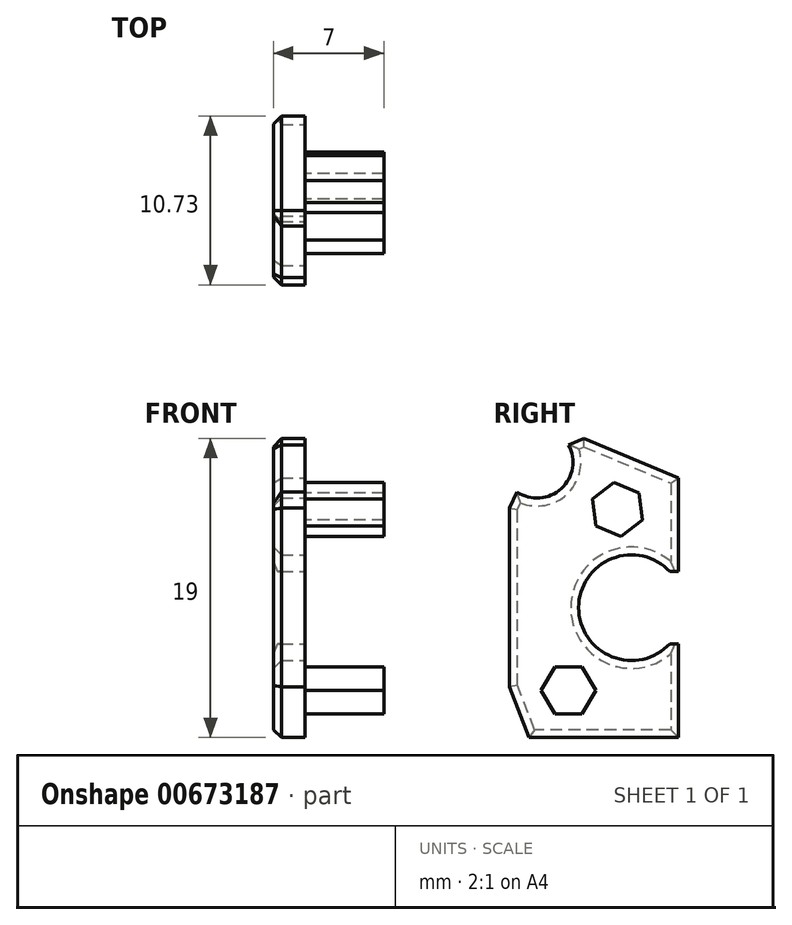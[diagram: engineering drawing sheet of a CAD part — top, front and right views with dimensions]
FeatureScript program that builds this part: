
annotation { "Feature Type Name" : "Feature", "Feature Type Description" : "" }
export const myFeature = defineFeature(function(context is Context, id is Id, definition is map)
    precondition{}
    {
        {
            var Q0;
            Q0=qCreatedBy(makeId("Right.planeOp"),FACE);
            var sketch = newSketch(context, id + "F0", { "sketchPlane" : qUnion([Q0])});
            skCircle(sketch, "E0.cCircle", {"center": v(1.33, 5.27) * mm, "radius": 1.5 * mm, "construction": true});
            skLineSegment(sketch, "E0.0", {"start": v(1.1, 6.99) * mm, "end": v(2.7, 6.32) * mm});
            skLineSegment(sketch, "E0.1", {"start": v(2.7, 6.32) * mm, "end": v(2.92, 4.6) * mm});
            skLineSegment(sketch, "E0.2", {"start": v(2.92, 4.6) * mm, "end": v(1.55, 3.55) * mm});
            skLineSegment(sketch, "E0.3", {"start": v(1.55, 3.55) * mm, "end": v(-0.05, 4.22) * mm});
            skLineSegment(sketch, "E0.4", {"start": v(-0.05, 4.22) * mm, "end": v(-0.27, 5.93) * mm});
            skLineSegment(sketch, "E0.5", {"start": v(-0.27, 5.93) * mm, "end": v(1.1, 6.99) * mm});
            skPoint(sketch, "E0.0.midPoint", {"position": v(1.9, 6.65) * mm});
            skCircle(sketch, "E1.cCircle", {"center": v(-1.8, -6.23) * mm, "radius": 1.5 * mm, "construction": true});
            skLineSegment(sketch, "E1.0", {"start": v(-0.92, -7.73) * mm, "end": v(-2.66, -7.73) * mm});
            skLineSegment(sketch, "E1.1", {"start": v(-2.66, -7.73) * mm, "end": v(-3.52, -6.23) * mm});
            skLineSegment(sketch, "E1.2", {"start": v(-3.52, -6.23) * mm, "end": v(-2.66, -4.73) * mm});
            skLineSegment(sketch, "E1.3", {"start": v(-2.66, -4.73) * mm, "end": v(-0.92, -4.73) * mm});
            skLineSegment(sketch, "E1.4", {"start": v(-0.92, -4.73) * mm, "end": v(-0.06, -6.23) * mm});
            skLineSegment(sketch, "E1.5", {"start": v(-0.06, -6.23) * mm, "end": v(-0.92, -7.73) * mm});
            skPoint(sketch, "E1.0.midPoint", {"position": v(-1.8, -7.73) * mm});
            skLineSegment(sketch, "E2", {"start": v(5.2, 1.3) * mm, "end": v(5.2, 7.27) * mm});
            skLineSegment(sketch, "E3", {"start": v(5.2, 7.27) * mm, "end": v(-0.8, 9.77) * mm});
            skLineSegment(sketch, "E4", {"start": v(-5.52, 5.37) * mm, "end": v(-5.52, -6) * mm});
            skLineSegment(sketch, "E5", {"start": v(-5.52, -6) * mm, "end": v(-4.3, -9.23) * mm});
            skLineSegment(sketch, "E6", {"start": v(-4.3, -9.23) * mm, "end": v(5.2, -9.23) * mm});
            skLineSegment(sketch, "E7", {"start": v(5.2, -9.23) * mm, "end": v(5.2, -3.27) * mm});
            skLineSegment(sketch, "E8", {"start": v(5.2, -3.27) * mm, "end": v(4.66, -3.27) * mm});
            skArc(sketch, "E9", {"start": v(4.66, 1.3) * mm, "mid": v(-1.14, -0.98) * mm, "end": v(4.66, -3.27) * mm});
            skArc(sketch, "E10", {"start": v(-5.05, 6.35) * mm, "mid": v(-2.24, 6.58) * mm, "end": v(-1.77, 9.36) * mm});
            skLineSegment(sketch, "E11", {"start": v(-5.52, 5.37) * mm, "end": v(-5.05, 6.35) * mm});
            skLineSegment(sketch, "E12", {"start": v(-0.8, 9.77) * mm, "end": v(-1.77, 9.36) * mm});
            skLineSegment(sketch, "E13", {"start": v(4.66, 1.3) * mm, "end": v(5.2, 1.3) * mm});
            skSolve(sketch);
        }
        {
            var Q0;
            Q0=qSketchRegion(id+"F0",true);
            var Q1;
            Q1=makeQuery(id+"F0.imprint","IMPRINT",FACE,{"disambiguationData":[TD([[makeQuery(id+"F0.imprint","IMPRINT",EDGE,{"derivedFrom":sQuery(id+"F0.wireOp",EDGE,"E1.0")}),-1.0]])]});
            var Q2;
            Q2=makeQuery(id+"F0.imprint","IMPRINT",FACE,{"disambiguationData":[TD([[makeQuery(id+"F0.imprint","IMPRINT",EDGE,{"derivedFrom":sQuery(id+"F0.wireOp",EDGE,"E0.0")}),-1.0]])]});
            extrude(context, id + "F1", {"entities" : qUnion([Q0, Q1, Q2]), "oppositeDirection" : true, "depth" : 2 * mm});
        }
        {
            var Q0;
            Q0=makeQuery(id+"F0.imprint","IMPRINT",FACE,{"disambiguationData":[TD([[makeQuery(id+"F0.imprint","IMPRINT",EDGE,{"derivedFrom":sQuery(id+"F0.wireOp",EDGE,"E0.0")}),-1.0]])]});
            var Q1;
            Q1=makeQuery(id+"F0.imprint","IMPRINT",FACE,{"disambiguationData":[TD([[makeQuery(id+"F0.imprint","IMPRINT",EDGE,{"derivedFrom":sQuery(id+"F0.wireOp",EDGE,"E1.0")}),-1.0]])]});
            extrude(context, id + "F2", {"entities" : qUnion([Q0, Q1]), "operationType" : NewBodyOperationType.ADD, "depth" : 5 * mm});
        }
        {
            var Q0;
            Q0=makeQuery(id+"F1.opExtrude","CAP_EDGE",EDGE,{"disambiguationData":[OSD([sQuery(id+"F0.wireOp",EDGE,"E4")])],"isStart":false});
            var Q1;
            Q1=makeQuery(id+"F1.opExtrude","CAP_EDGE",EDGE,{"disambiguationData":[OSD([sQuery(id+"F0.wireOp",EDGE,"E5")])],"isStart":false});
            var Q2;
            Q2=makeQuery(id+"F1.opExtrude","CAP_EDGE",EDGE,{"disambiguationData":[OSD([sQuery(id+"F0.wireOp",EDGE,"E11")])],"isStart":false});
            var Q3;
            Q3=makeQuery(id+"F1.opExtrude","CAP_EDGE",EDGE,{"disambiguationData":[OSD([sQuery(id+"F0.wireOp",EDGE,"E10")])],"isStart":false});
            var Q4;
            Q4=makeQuery(id+"F1.opExtrude","CAP_FACE",FACE,{"disambiguationData":[OSD([sQuery(id+"F0.wireOp",EDGE,"E2"),sQuery(id+"F0.wireOp",EDGE,"E3"),sQuery(id+"F0.wireOp",EDGE,"E4"),sQuery(id+"F0.wireOp",EDGE,"E5"),sQuery(id+"F0.wireOp",EDGE,"E6"),sQuery(id+"F0.wireOp",EDGE,"E7"),sQuery(id+"F0.wireOp",EDGE,"E8"),sQuery(id+"F0.wireOp",EDGE,"E9"),sQuery(id+"F0.wireOp",EDGE,"E10"),sQuery(id+"F0.wireOp",EDGE,"E11"),sQuery(id+"F0.wireOp",EDGE,"E12"),sQuery(id+"F0.wireOp",EDGE,"E13")])],"isStart":false});
            chamfer(context, id + "F3", {"entities" : qUnion([Q0, Q1, Q2, Q3, Q4]), "width" : .5 * mm, "tangentPropagation" : true});
        }
    });
